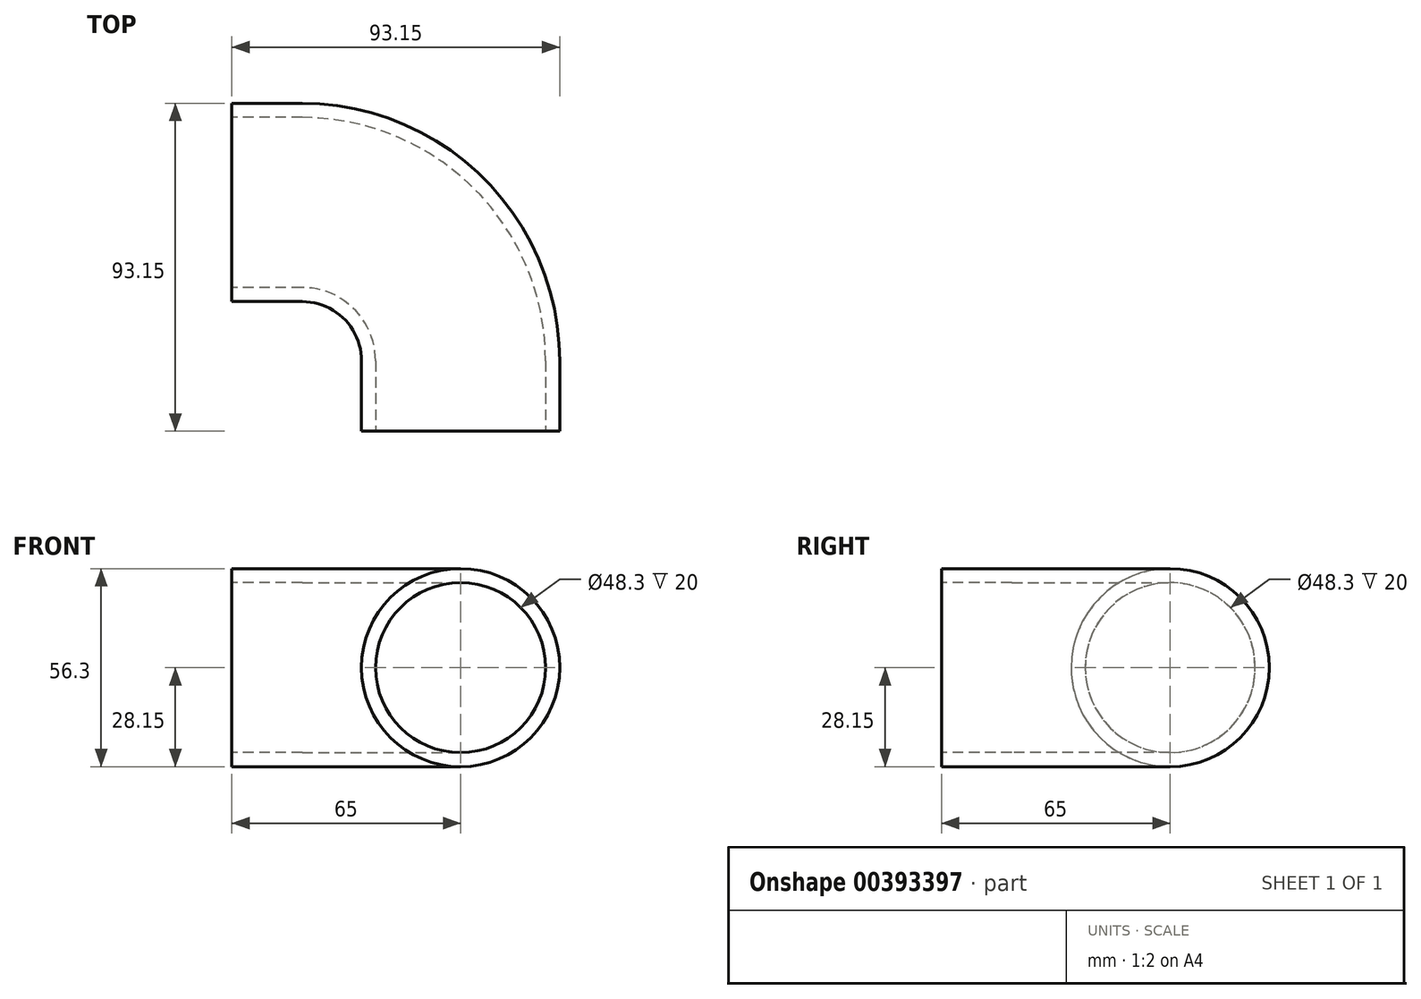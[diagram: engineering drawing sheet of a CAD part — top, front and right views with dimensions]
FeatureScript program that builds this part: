
annotation { "Feature Type Name" : "Feature", "Feature Type Description" : "" }
export const myFeature = defineFeature(function(context is Context, id is Id, definition is map)
    precondition{}
    {
        {
            var Q0;
            Q0=qCreatedBy(makeId("Top.planeOp"),FACE);
            var sketch = newSketch(context, id + "F0", { "sketchPlane" : qUnion([Q0])});
            skArc(sketch, "E0", {"start": v(25, 0) * mm, "mid": v(17.68, 17.68) * mm, "end": v(0, 25) * mm});
            skLineSegment(sketch, "E1", {"start": v(0, 25) * mm, "end": v(-20, 25) * mm});
            skLineSegment(sketch, "E2", {"start": v(25, 0) * mm, "end": v(25, -20) * mm});
            skSolve(sketch);
        }
        {
            var Q0;
            Q0=qCreatedBy(makeId("Right.planeOp"),FACE);
            var sketch = newSketch(context, id + "F1", { "sketchPlane" : qUnion([Q0])});
            skPoint(sketch, "E3.0", {"position": v(45, 0) * mm});
            skCircle(sketch, "E4", {"center": v(45, 0) * mm, "radius": 24.15 * mm});
            skCircle(sketch, "E5.0", {"center": v(45, 0) * mm, "radius": 28.15 * mm});
            skSolve(sketch);
        }
        {
            var Q0;
            Q0=makeQuery(id+"F1.imprint","IMPRINT",FACE,{"disambiguationData":[TD([[makeQuery(id+"F1.imprint","IMPRINT",EDGE,{"derivedFrom":sQuery(id+"F1.wireOp",EDGE,"E4")}),-1.0]])]});
            var Q1;
            Q1=sQuery(id+"F0.wireOp",EDGE,"E0");
            var Q2;
            Q2=sQuery(id+"F0.wireOp",EDGE,"E2");
            sweep(context, id + "F2", {"profiles" : qUnion([Q0]), "path" : qUnion([Q1, Q2])});
        }
        {
            var Q0;
            Q0=makeQuery(id+"F2.opSweep","CAP_FACE",FACE,{"disambiguationData":[OSD([sQuery(id+"F0.wireOp",VERTEX,"E0.end"),sQuery(id+"F1.wireOp",EDGE,"E4"),sQuery(id+"F1.wireOp",EDGE,"E5.0")])],"isStart":true});
            var Q1;
            Q1=sQuery(id+"F0.wireOp",EDGE,"E1");
            sweep(context, id + "F3", {"operationType" : NewBodyOperationType.ADD, "profiles" : qUnion([Q0]), "path" : qUnion([Q1])});
        }
    });
